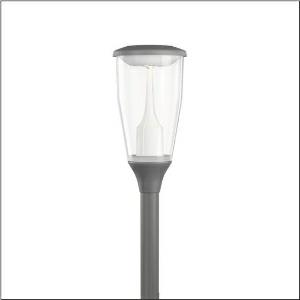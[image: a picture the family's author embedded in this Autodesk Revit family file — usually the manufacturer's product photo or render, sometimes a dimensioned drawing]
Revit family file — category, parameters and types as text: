
# Revit family: dl_11_iq___st1_2a_5xa5575kf14hp00022_6351
name_source: partatom
category: Lighting Fixtures
units: mm (PartAtom-declared; Revit-internal decimal feet)

## family parameters
Cut with Voids When Loaded = No
Host = Face
Light Source = No
Part Type = Normal
Room Calculation Point = No
Round Connector Dimension = Use Diameter
Shared = No

## types (1)
- --- (1 x LED, 5060 lm, 33.6 W, 4000K)
    Apparent Load = 34 VA
    CIE Flux Codes = 23 60 93 95 100
    Color Rendering = 70
    Color Temperature = 4000K
    Default Elevation = 1800 mm
    Description = DL 11 iQ, mast luminaire, Module 540 iQ-SR, primary light control with 3 zone facetted reflector, of plastic, silver coated, highly specular, structured, primary optical cover: cover, of PMMA, transparent, light distribution: ST1.2a, light emission: direct distribution, primary light characteristic: asymmetric, installation type: post-top, LED, High Power LED, light colour: 740, colour temperature: 4000K, control gear: iQ Street-Remote, control: Street-Remote, Auto-Match, Temp-Guard, Lumen-Switch, Night-Set, Smart-Wire, Light-Fading, Desk-Remote (wireless, voltage-free reading and setting of iQ features in the workshop via application-optimized NFC function/RFID function), optimised constant luminous flux control (CLO 2.0), mains connection: 220..240V, AC, 50/60Hz, connection cable pre-assembled, cable length: 5,5m, wiring characteristics: H07RN-F, 5-core, 1.5mm², start of lifetime: 34W, end of service life: 36W, luminaire housing, upper part, of diecast aluminium, coated, SITECO metallic grey (DB 702S), spigot size: 76mm (post-top), mounting height: 3..5m, post-top mast mounting element, of diecast aluminium, coated, SITECO metallic grey (DB 702S), Module 540 iQ-SR, traffic white (RAL 9016), equipment: Power, protection rating (complete): IP66, insulation class (complete): insulation class II (safety insulation), certification: CE, ENEC, ENEC+, VDE, impact resistance: IK07, packaging unit: 1 piece

Light Distribution: ST1.2a
    Height = 665 mm
    Lamp = 1 x LED
    Lamp Light Flux = 5060 lm
    Lamp Power = 33.6 W
    Lamp count = 1
    Length = 334 mm
    Luminous efficacy = 151 lm/W
    Manufacturer = Siteco
    ModVariant = No
    Model = 5XA5575KF14HP00022
    Number of Poles = 1
    OnlyDefault = Yes
    Power Factor = 1
    Product Name = DL 11 iQ | ST1.2a
    Product group = mast luminaire | pylon top
    ProductGroupID = 6100
    Protection Class = Protection class II
    Protection Degree = IP 66
    RLX_Detail_Level = 1
    RLX_Emergency_Light_Flux = 0 lm
    RLX_Emergency_Type = 0
    RLX_Emergency_Type_DB = No
    RlxData = <blob elided: 160577 chars, md5=6760fad4>
    Socket = socket
    Standby Power = 0 W
    System Light Flux = 5060 lm
    System Power = 34 W
    Type Comments = factory setting: luminous flux: 100 % | dim-lin: 254 | 695 mA
    Type Image = l_1258354.jpg
    URL = http://relux.com
    VarID = @adj_040121
    Voltage = 0 V
    Weight = 0.00 kg
    Width = 0 mm  [stored 0 ft]

note: [stored X ft] marks values corroborated as IEEE doubles in the binary element streams (Revit-internal decimal feet)

## geometry (parser evidence)
native form markers: Blend x4, Sweep x10
no freeform markers — native parametric forms only
